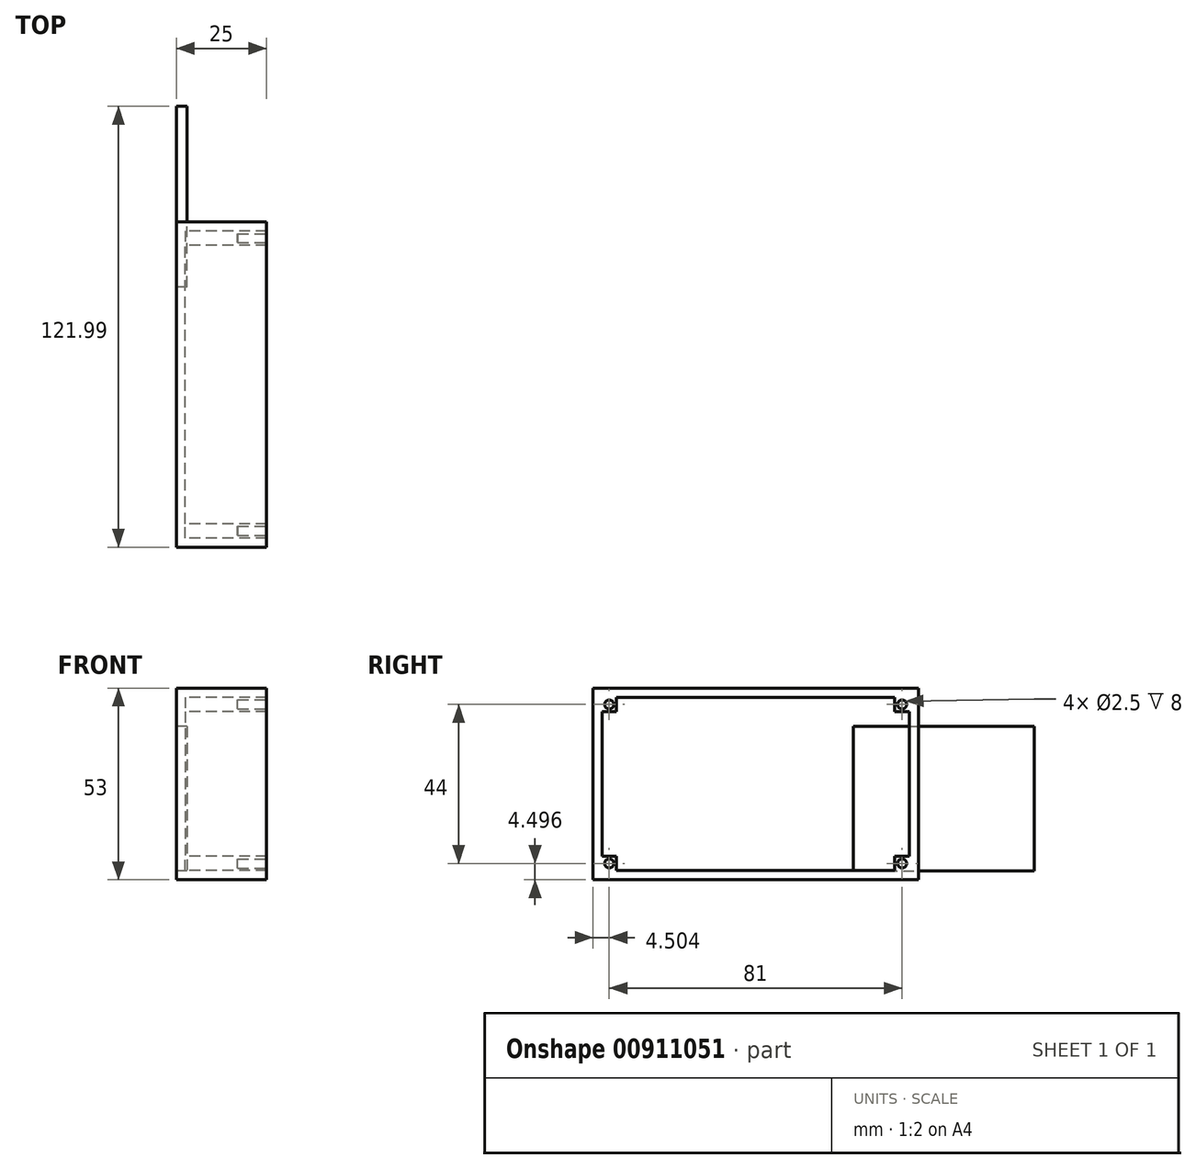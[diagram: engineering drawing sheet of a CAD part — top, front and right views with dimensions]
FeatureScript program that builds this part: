
annotation { "Feature Type Name" : "Feature", "Feature Type Description" : "" }
export const myFeature = defineFeature(function(context is Context, id is Id, definition is map)
    precondition{}
    {
        {
            var Q0;
            Q0=qCreatedBy(makeId("Right.planeOp"),FACE);
            var sketch = newSketch(context, id + "F0", { "sketchPlane" : qUnion([Q0])});
            skLineSegment(sketch, "E0.bottom", {"start": v(-59.79, 62.36) * mm, "end": v(30.21, 62.36) * mm});
            skLineSegment(sketch, "E0.top", {"start": v(-59.79, 9.36) * mm, "end": v(30.21, 9.36) * mm});
            skLineSegment(sketch, "E0.left", {"start": v(-59.79, 62.36) * mm, "end": v(-59.79, 9.36) * mm});
            skLineSegment(sketch, "E0.right", {"start": v(30.21, 62.36) * mm, "end": v(30.21, 9.36) * mm});
            skSolve(sketch);
        }
        {
            var Q0;
            Q0=makeQuery(id+"F0.imprint","IMPRINT",FACE,{"disambiguationData":[TD([[makeQuery(id+"F0.imprint","IMPRINT",EDGE,{"derivedFrom":sQuery(id+"F0.wireOp",EDGE,"E0.bottom")}),-1.0]])]});
            extrude(context, id + "F1", {"entities" : qUnion([Q0]), "depth" : 25 * mm, "offsetDistance" : 25 * mm});
        }
        {
            var Q0;
            Q0=makeQuery(id+"F1.opExtrude","CAP_FACE",FACE,{"disambiguationData":[OSD([sQuery(id+"F0.wireOp",EDGE,"E0.bottom"),sQuery(id+"F0.wireOp",EDGE,"E0.top"),sQuery(id+"F0.wireOp",EDGE,"E0.left"),sQuery(id+"F0.wireOp",EDGE,"E0.right")])],"isStart":false});
            shell(context, id + "F2", {"entities" : qUnion([Q0]), "thickness" : 2.5 * mm});
        }
        {
            var Q0;
            Q0=makeQuery(id+"F2.opShell","OFFSET_FACE",FACE,{"disambiguationData":[OSD([sQuery(id+"F0.wireOp",EDGE,"E0.bottom"),sQuery(id+"F0.wireOp",EDGE,"E0.top"),sQuery(id+"F0.wireOp",EDGE,"E0.left"),sQuery(id+"F0.wireOp",EDGE,"E0.right")])]});
            var sketch = newSketch(context, id + "F3", { "sketchPlane" : qUnion([Q0])});
            skLineSegment(sketch, "E1.bottom", {"start": v(-57.29, 59.86) * mm, "end": v(-53.29, 59.86) * mm});
            skLineSegment(sketch, "E1.top", {"start": v(-57.29, 55.86) * mm, "end": v(-53.29, 55.86) * mm});
            skLineSegment(sketch, "E1.left", {"start": v(-57.29, 59.86) * mm, "end": v(-57.29, 55.86) * mm});
            skLineSegment(sketch, "E1.right", {"start": v(-53.29, 59.86) * mm, "end": v(-53.29, 55.86) * mm});
            skSolve(sketch);
        }
        {
            var Q0;
            Q0=makeQuery(id+"F3.imprint","IMPRINT",FACE,{"disambiguationData":[TD([[makeQuery(id+"F3.imprint","IMPRINT",EDGE,{"derivedFrom":sQuery(id+"F3.wireOp",EDGE,"E1.bottom")}),-1.0]])]});
            extrude(context, id + "F4", {"entities" : qUnion([Q0]), "operationType" : NewBodyOperationType.ADD, "depth" : 22.5 * mm, "offsetDistance" : 25 * mm});
        }
        {
            var Q0;
            Q0=makeQuery(id+"F2.opShell","OFFSET_FACE",FACE,{"disambiguationData":[OSD([sQuery(id+"F0.wireOp",EDGE,"E0.bottom"),sQuery(id+"F0.wireOp",EDGE,"E0.top"),sQuery(id+"F0.wireOp",EDGE,"E0.left"),sQuery(id+"F0.wireOp",EDGE,"E0.right")])]});
            var sketch = newSketch(context, id + "F5", { "sketchPlane" : qUnion([Q0])});
            skLineSegment(sketch, "E2.bottom", {"start": v(-57.29, 11.86) * mm, "end": v(-53.29, 11.86) * mm});
            skLineSegment(sketch, "E2.top", {"start": v(-57.29, 15.86) * mm, "end": v(-53.29, 15.86) * mm});
            skLineSegment(sketch, "E2.left", {"start": v(-57.29, 11.86) * mm, "end": v(-57.29, 15.86) * mm});
            skLineSegment(sketch, "E2.right", {"start": v(-53.29, 11.86) * mm, "end": v(-53.29, 15.86) * mm});
            skSolve(sketch);
        }
        {
            var Q0;
            Q0=makeQuery(id+"F5.imprint","IMPRINT",FACE,{"disambiguationData":[TD([[makeQuery(id+"F5.imprint","IMPRINT",EDGE,{"derivedFrom":sQuery(id+"F5.wireOp",EDGE,"E2.bottom")}),1.0]])]});
            extrude(context, id + "F6", {"entities" : qUnion([Q0]), "operationType" : NewBodyOperationType.ADD, "depth" : 22.5 * mm, "offsetDistance" : 25 * mm});
        }
        {
            var Q0;
            Q0=makeQuery(id+"F2.opShell","OFFSET_FACE",FACE,{"disambiguationData":[OSD([sQuery(id+"F0.wireOp",EDGE,"E0.bottom"),sQuery(id+"F0.wireOp",EDGE,"E0.top"),sQuery(id+"F0.wireOp",EDGE,"E0.left"),sQuery(id+"F0.wireOp",EDGE,"E0.right")])]});
            var sketch = newSketch(context, id + "F7", { "sketchPlane" : qUnion([Q0])});
            skLineSegment(sketch, "E3.bottom", {"start": v(27.71, 59.86) * mm, "end": v(23.71, 59.86) * mm});
            skLineSegment(sketch, "E3.top", {"start": v(27.71, 55.86) * mm, "end": v(23.71, 55.86) * mm});
            skLineSegment(sketch, "E3.left", {"start": v(27.71, 59.86) * mm, "end": v(27.71, 55.86) * mm});
            skLineSegment(sketch, "E3.right", {"start": v(23.71, 59.86) * mm, "end": v(23.71, 55.86) * mm});
            skLineSegment(sketch, "E4.bottom", {"start": v(27.71, 11.86) * mm, "end": v(23.71, 11.86) * mm});
            skLineSegment(sketch, "E4.top", {"start": v(27.71, 15.86) * mm, "end": v(23.71, 15.86) * mm});
            skLineSegment(sketch, "E4.left", {"start": v(27.71, 11.86) * mm, "end": v(27.71, 15.86) * mm});
            skLineSegment(sketch, "E4.right", {"start": v(23.71, 11.86) * mm, "end": v(23.71, 15.86) * mm});
            skSolve(sketch);
        }
        {
            var Q0;
            Q0=makeQuery(id+"F7.imprint","IMPRINT",FACE,{"disambiguationData":[TD([[makeQuery(id+"F7.imprint","IMPRINT",EDGE,{"derivedFrom":sQuery(id+"F7.wireOp",EDGE,"E3.bottom")}),-1.0]])]});
            var Q1;
            Q1=makeQuery(id+"F7.imprint","IMPRINT",FACE,{"disambiguationData":[TD([[makeQuery(id+"F7.imprint","IMPRINT",EDGE,{"derivedFrom":sQuery(id+"F7.wireOp",EDGE,"E4.bottom")}),1.0]])]});
            extrude(context, id + "F8", {"entities" : qUnion([Q0, Q1]), "operationType" : NewBodyOperationType.ADD, "depth" : 22.5 * mm, "offsetDistance" : 25 * mm});
        }
        {
            var Q0;
            Q0=makeQuery(id+"F8.boolean.opBoolean","MERGE",FACE,{"derivedFrom":[makeQuery(id+"F6.boolean.opBoolean","MERGE",FACE,{"derivedFrom":[makeQuery(id+"F4.boolean.opBoolean","MERGE",FACE,{"derivedFrom":[makeQuery(id+"F1.opExtrude","CAP_FACE",FACE,{"disambiguationData":[OSD([sQuery(id+"F0.wireOp",EDGE,"E0.bottom"),sQuery(id+"F0.wireOp",EDGE,"E0.top"),sQuery(id+"F0.wireOp",EDGE,"E0.left"),sQuery(id+"F0.wireOp",EDGE,"E0.right")])],"isStart":false}),makeQuery(id+"F4.opExtrude","CAP_FACE",FACE,{"disambiguationData":[OSD([sQuery(id+"F3.wireOp",EDGE,"E1.bottom"),sQuery(id+"F3.wireOp",EDGE,"E1.top"),sQuery(id+"F3.wireOp",EDGE,"E1.left"),sQuery(id+"F3.wireOp",EDGE,"E1.right")])],"isStart":false})]}),makeQuery(id+"F6.opExtrude","CAP_FACE",FACE,{"disambiguationData":[OSD([sQuery(id+"F5.wireOp",EDGE,"E2.bottom"),sQuery(id+"F5.wireOp",EDGE,"E2.top"),sQuery(id+"F5.wireOp",EDGE,"E2.left"),sQuery(id+"F5.wireOp",EDGE,"E2.right")])],"isStart":false})]}),makeQuery(id+"F8.opExtrude","CAP_FACE",FACE,{"disambiguationData":[OSD([sQuery(id+"F7.wireOp",EDGE,"E3.bottom"),sQuery(id+"F7.wireOp",EDGE,"E3.top"),sQuery(id+"F7.wireOp",EDGE,"E3.left"),sQuery(id+"F7.wireOp",EDGE,"E3.right")])],"isStart":false}),makeQuery(id+"F8.opExtrude","CAP_FACE",FACE,{"disambiguationData":[OSD([sQuery(id+"F7.wireOp",EDGE,"E4.bottom"),sQuery(id+"F7.wireOp",EDGE,"E4.top"),sQuery(id+"F7.wireOp",EDGE,"E4.left"),sQuery(id+"F7.wireOp",EDGE,"E4.right")])],"isStart":false})]});
            var sketch = newSketch(context, id + "F9", { "sketchPlane" : qUnion([Q0])});
            skCircle(sketch, "E5", {"center": v(25.71, 13.86) * mm, "radius": 1.25 * mm});
            skPoint(sketch, "E5.centerSnap0", {"position": v(23.71, 13.86) * mm});
            skPoint(sketch, "E5.centerSnap1", {"position": v(25.71, 15.86) * mm});
            skCircle(sketch, "E6", {"center": v(25.71, 57.86) * mm, "radius": 1.25 * mm});
            skPoint(sketch, "E6.centerSnap0", {"position": v(25.71, 55.86) * mm});
            skPoint(sketch, "E6.centerSnap1", {"position": v(23.71, 57.86) * mm});
            skCircle(sketch, "E7", {"center": v(-55.29, 13.86) * mm, "radius": 1.25 * mm});
            skPoint(sketch, "E7.centerSnap0", {"position": v(-53.29, 13.86) * mm});
            skPoint(sketch, "E7.centerSnap1", {"position": v(-55.29, 15.86) * mm});
            skCircle(sketch, "E8", {"center": v(-55.29, 57.86) * mm, "radius": 1.25 * mm});
            skPoint(sketch, "E8.centerSnap0", {"position": v(-53.29, 57.86) * mm});
            skPoint(sketch, "E8.centerSnap1", {"position": v(-55.29, 55.86) * mm});
            skSolve(sketch);
        }
        {
            var Q0;
            Q0 = qSketchRegion(id + "F9", true);
            extrude(context, id + "F10", {"entities" : qUnion([Q0]), "operationType" : NewBodyOperationType.REMOVE, "oppositeDirection" : true, "depth" : 8 * mm, "offsetDistance" : 25 * mm});
        }
        {
            var Q0;
            Q0=qCreatedBy(makeId("Right.planeOp"),FACE);
            var sketch = newSketch(context, id + "F11", { "sketchPlane" : qUnion([Q0])});
            skLineSegment(sketch, "E9.bottom", {"start": v(12.2, 51.8) * mm, "end": v(62.2, 51.8) * mm});
            skLineSegment(sketch, "E9.top", {"start": v(12.2, 11.8) * mm, "end": v(62.2, 11.8) * mm});
            skLineSegment(sketch, "E9.left", {"start": v(12.2, 51.8) * mm, "end": v(12.2, 11.8) * mm});
            skLineSegment(sketch, "E9.right", {"start": v(62.2, 51.8) * mm, "end": v(62.2, 11.8) * mm});
            skSolve(sketch);
        }
        {
            var Q0;
            Q0=makeQuery(id+"F11.imprint","IMPRINT",FACE,{"disambiguationData":[TD([[makeQuery(id+"F11.imprint","IMPRINT",EDGE,{"derivedFrom":sQuery(id+"F11.wireOp",EDGE,"E9.bottom")}),-1.0]])]});
            extrude(context, id + "F12", {"entities" : qUnion([Q0]), "depth" : 3 * mm, "offsetDistance" : 25 * mm});
        }
    });
